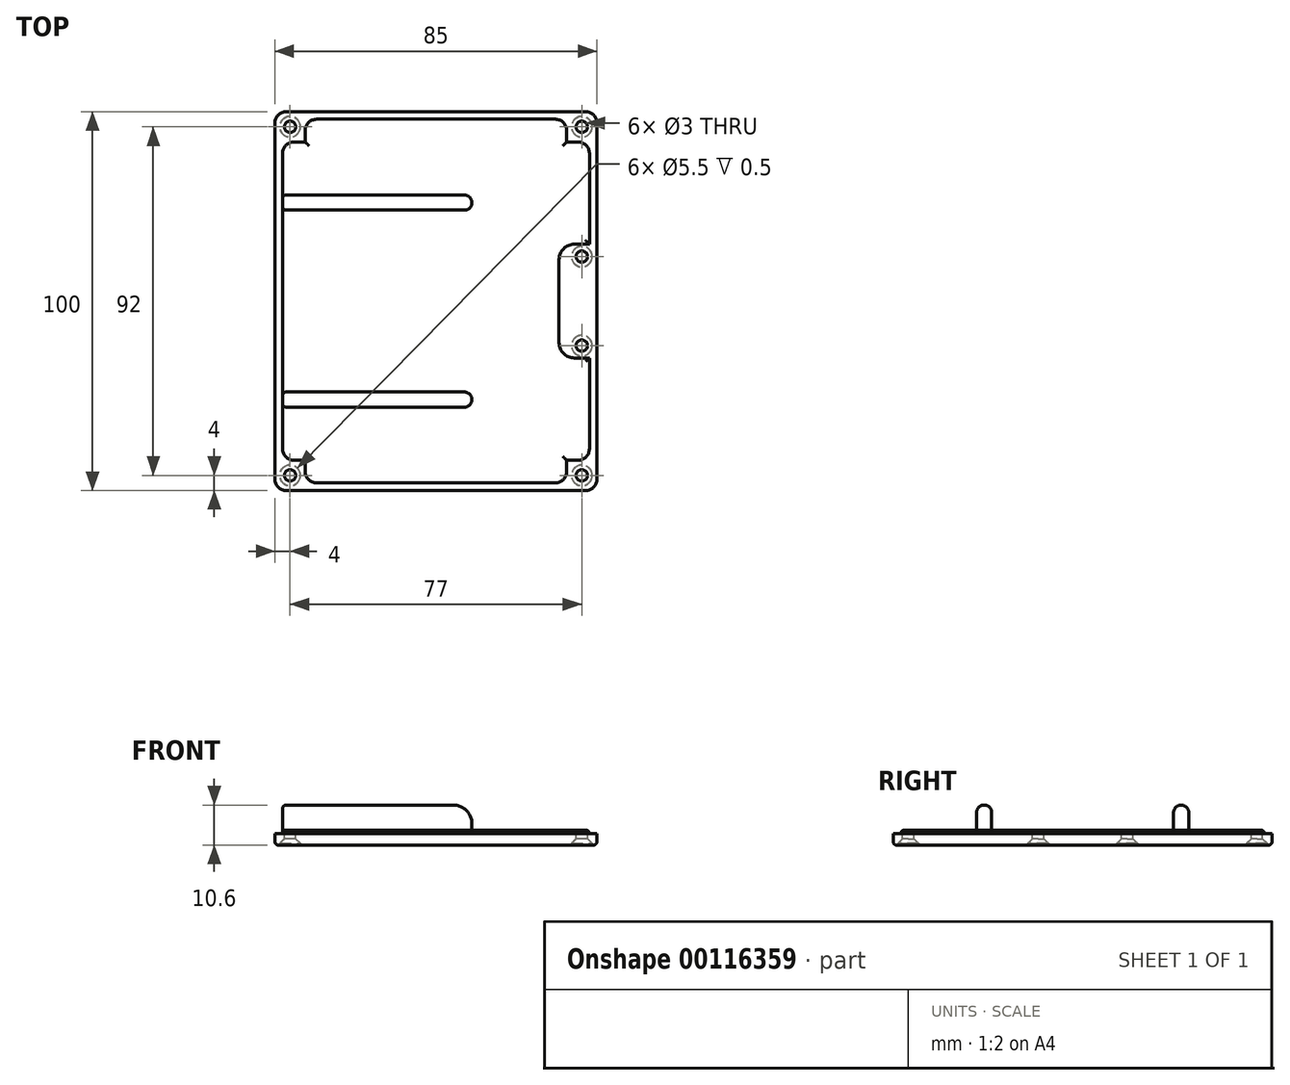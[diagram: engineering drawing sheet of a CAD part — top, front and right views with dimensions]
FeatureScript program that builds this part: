
annotation { "Feature Type Name" : "Feature", "Feature Type Description" : "" }
export const myFeature = defineFeature(function(context is Context, id is Id, definition is map)
    precondition{}
    {
        {
            var Q0;
            Q0=qCreatedBy(makeId("Top.planeOp"),FACE);
            var sketch = newSketch(context, id + "F0", { "sketchPlane" : qUnion([Q0])});
            skLineSegment(sketch, "E0.bottom", {"start": v(3, 0) * mm, "end": v(82, 0) * mm});
            skLineSegment(sketch, "E0.top", {"start": v(3, 100) * mm, "end": v(82, 100) * mm});
            skLineSegment(sketch, "E0.left", {"start": v(0, 3) * mm, "end": v(0, 97) * mm});
            skLineSegment(sketch, "E0.right", {"start": v(85, 3) * mm, "end": v(85, 97) * mm});
            skPoint(sketch, "E1.visualSharp", {"position": v(0, 100) * mm});
            skArc(sketch, "E1.filletArc", {"start": v(3, 100) * mm, "mid": v(0.88, 99.12) * mm, "end": v(0, 97) * mm});
            skPoint(sketch, "E2.visualSharp", {"position": v(85, 100) * mm});
            skArc(sketch, "E2.filletArc", {"start": v(85, 97) * mm, "mid": v(84.12, 99.12) * mm, "end": v(82, 100) * mm});
            skPoint(sketch, "E3.visualSharp", {"position": v(85, 0) * mm});
            skArc(sketch, "E3.filletArc", {"start": v(82, 0) * mm, "mid": v(84.12, 0.88) * mm, "end": v(85, 3) * mm});
            skPoint(sketch, "E4.visualSharp", {"position": v(0, 0) * mm});
            skArc(sketch, "E4.filletArc", {"start": v(0, 3) * mm, "mid": v(0.88, 0.88) * mm, "end": v(3, 0) * mm});
            skSolve(sketch);
        }
        {
            var Q0;
            Q0=makeQuery(id+"F0.imprint","IMPRINT",FACE,{"disambiguationData":[TD([[makeQuery(id+"F0.imprint","IMPRINT",EDGE,{"derivedFrom":sQuery(id+"F0.wireOp",EDGE,"E0.bottom")}),1.0]])]});
            extrude(context, id + "F1", {"entities" : qUnion([Q0]), "depth" : 3 * mm});
        }
        {
            var Q0;
            Q0=makeQuery(id+"F1.opExtrude","CAP_FACE",FACE,{"disambiguationData":[OSD([sQuery(id+"F0.wireOp",EDGE,"E0.bottom"),sQuery(id+"F0.wireOp",EDGE,"E0.top"),sQuery(id+"F0.wireOp",EDGE,"E0.left"),sQuery(id+"F0.wireOp",EDGE,"E0.right"),sQuery(id+"F0.wireOp",EDGE,"E1.filletArc"),sQuery(id+"F0.wireOp",EDGE,"E2.filletArc"),sQuery(id+"F0.wireOp",EDGE,"E3.filletArc"),sQuery(id+"F0.wireOp",EDGE,"E4.filletArc")])],"isStart":false});
            var sketch = newSketch(context, id + "F2", { "sketchPlane" : qUnion([Q0])});
            skCircle(sketch, "E5", {"center": v(4, 96) * mm, "radius": 1.5 * mm});
            skCircle(sketch, "E6", {"center": v(81, 96) * mm, "radius": 1.5 * mm});
            skCircle(sketch, "E7", {"center": v(81, 4) * mm, "radius": 1.5 * mm});
            skCircle(sketch, "E8", {"center": v(4, 4) * mm, "radius": 1.5 * mm});
            skCircle(sketch, "E9", {"center": v(81, 61.75) * mm, "radius": 1.5 * mm});
            skCircle(sketch, "E10", {"center": v(81, 38.25) * mm, "radius": 1.5 * mm});
            skSolve(sketch);
        }
        {
            var Q0;
            Q0=makeQuery(id+"F2.imprint","IMPRINT",FACE,{"disambiguationData":[TD([[makeQuery(id+"F2.imprint","IMPRINT",EDGE,{"derivedFrom":sQuery(id+"F2.wireOp",EDGE,"E5")}),1.0]])]});
            var Q1;
            Q1=makeQuery(id+"F2.imprint","IMPRINT",FACE,{"disambiguationData":[TD([[makeQuery(id+"F2.imprint","IMPRINT",EDGE,{"derivedFrom":sQuery(id+"F2.wireOp",EDGE,"E6")}),1.0]])]});
            var Q2;
            Q2=makeQuery(id+"F2.imprint","IMPRINT",FACE,{"disambiguationData":[TD([[makeQuery(id+"F2.imprint","IMPRINT",EDGE,{"derivedFrom":sQuery(id+"F2.wireOp",EDGE,"E8")}),1.0]])]});
            var Q3;
            Q3=makeQuery(id+"F2.imprint","IMPRINT",FACE,{"disambiguationData":[TD([[makeQuery(id+"F2.imprint","IMPRINT",EDGE,{"derivedFrom":sQuery(id+"F2.wireOp",EDGE,"E7")}),1.0]])]});
            var Q4;
            Q4=makeQuery(id+"F2.imprint","IMPRINT",FACE,{"disambiguationData":[TD([[makeQuery(id+"F2.imprint","IMPRINT",EDGE,{"derivedFrom":sQuery(id+"F2.wireOp",EDGE,"E9")}),1.0]])]});
            var Q5;
            Q5=makeQuery(id+"F2.imprint","IMPRINT",FACE,{"disambiguationData":[TD([[makeQuery(id+"F2.imprint","IMPRINT",EDGE,{"derivedFrom":sQuery(id+"F2.wireOp",EDGE,"E10")}),1.0]])]});
            extrude(context, id + "F3", {"entities" : qUnion([Q0, Q1, Q2, Q3, Q4, Q5]), "operationType" : NewBodyOperationType.REMOVE, "oppositeDirection" : true, "depth" : 5 * mm});
        }
        {
            var Q0;
            Q0=makeQuery(id+"F1.opExtrude","CAP_FACE",FACE,{"disambiguationData":[OSD([sQuery(id+"F0.wireOp",EDGE,"E0.bottom"),sQuery(id+"F0.wireOp",EDGE,"E0.top"),sQuery(id+"F0.wireOp",EDGE,"E0.left"),sQuery(id+"F0.wireOp",EDGE,"E0.right"),sQuery(id+"F0.wireOp",EDGE,"E1.filletArc"),sQuery(id+"F0.wireOp",EDGE,"E2.filletArc"),sQuery(id+"F0.wireOp",EDGE,"E3.filletArc"),sQuery(id+"F0.wireOp",EDGE,"E4.filletArc")])],"isStart":false});
            var sketch = newSketch(context, id + "F4", { "sketchPlane" : qUnion([Q0])});
            skLineSegment(sketch, "E11.1", {"start": v(11, 2) * mm, "end": v(74, 2) * mm});
            skLineSegment(sketch, "E11.2", {"start": v(2, 11) * mm, "end": v(2, 89) * mm});
            skLineSegment(sketch, "E11.5", {"start": v(11, 98) * mm, "end": v(74, 98) * mm});
            skLineSegment(sketch, "E11.7", {"start": v(83, 11) * mm, "end": v(83, 35) * mm});
            skLineSegment(sketch, "E12.top", {"start": v(5, 92) * mm, "end": v(8, 92) * mm});
            skLineSegment(sketch, "E12.right", {"start": v(8, 95) * mm, "end": v(8, 92) * mm});
            skLineSegment(sketch, "E13.top", {"start": v(80, 92) * mm, "end": v(77, 92) * mm});
            skLineSegment(sketch, "E13.right", {"start": v(77, 95) * mm, "end": v(77, 92) * mm});
            skLineSegment(sketch, "E14.top", {"start": v(80, 8) * mm, "end": v(77, 8) * mm});
            skLineSegment(sketch, "E14.right", {"start": v(77, 5) * mm, "end": v(77, 8) * mm});
            skLineSegment(sketch, "E15.top", {"start": v(5, 8) * mm, "end": v(8, 8) * mm});
            skLineSegment(sketch, "E15.right", {"start": v(8, 5) * mm, "end": v(8, 8) * mm});
            skPoint(sketch, "E16.visualSharp", {"position": v(2, 92) * mm});
            skArc(sketch, "E16.filletArc", {"start": v(5, 92) * mm, "mid": v(2.88, 91.12) * mm, "end": v(2, 89) * mm});
            skPoint(sketch, "E17.visualSharp", {"position": v(8, 98) * mm});
            skArc(sketch, "E17.filletArc", {"start": v(11, 98) * mm, "mid": v(8.88, 97.12) * mm, "end": v(8, 95) * mm});
            skPoint(sketch, "E18.visualSharp", {"position": v(77, 98) * mm});
            skArc(sketch, "E18.filletArc", {"start": v(77, 95) * mm, "mid": v(76.12, 97.12) * mm, "end": v(74, 98) * mm});
            skPoint(sketch, "E19.visualSharp", {"position": v(83, 92) * mm});
            skArc(sketch, "E19.filletArc", {"start": v(83, 89) * mm, "mid": v(82.12, 91.12) * mm, "end": v(80, 92) * mm});
            skPoint(sketch, "E20.visualSharp", {"position": v(83, 8) * mm});
            skArc(sketch, "E20.filletArc", {"start": v(80, 8) * mm, "mid": v(82.12, 8.88) * mm, "end": v(83, 11) * mm});
            skPoint(sketch, "E21.visualSharp", {"position": v(77, 2) * mm});
            skArc(sketch, "E21.filletArc", {"start": v(74, 2) * mm, "mid": v(76.12, 2.88) * mm, "end": v(77, 5) * mm});
            skPoint(sketch, "E22.visualSharp", {"position": v(8, 2) * mm});
            skArc(sketch, "E22.filletArc", {"start": v(8, 5) * mm, "mid": v(8.88, 2.88) * mm, "end": v(11, 2) * mm});
            skPoint(sketch, "E23.visualSharp", {"position": v(2, 8) * mm});
            skArc(sketch, "E23.filletArc", {"start": v(2, 11) * mm, "mid": v(2.88, 8.88) * mm, "end": v(5, 8) * mm});
            skLineSegment(sketch, "E24.bottom", {"start": v(83, 50) * mm, "end": v(75, 50) * mm, "construction": true});
            skLineSegment(sketch, "E24.top", {"start": v(83, 65) * mm, "end": v(75, 65) * mm, "construction": true});
            skLineSegment(sketch, "E24.right", {"start": v(75, 50) * mm, "end": v(75, 65) * mm, "construction": true});
            skLineSegment(sketch, "E25.top", {"start": v(83, 35) * mm, "end": v(75, 35) * mm, "construction": true});
            skLineSegment(sketch, "E25.right", {"start": v(75, 50) * mm, "end": v(75, 35) * mm, "construction": true});
            skLineSegment(sketch, "E26.bottom", {"start": v(83, 65) * mm, "end": v(79, 65) * mm});
            skLineSegment(sketch, "E26.top", {"start": v(83, 35) * mm, "end": v(79, 35) * mm});
            skLineSegment(sketch, "E26.right", {"start": v(75, 61) * mm, "end": v(75, 39) * mm});
            skLineSegment(sketch, "E27.trimOffspring", {"start": v(83, 65) * mm, "end": v(83, 89) * mm});
            skPoint(sketch, "E28.visualSharp", {"position": v(75, 65) * mm});
            skArc(sketch, "E28.filletArc", {"start": v(79, 65) * mm, "mid": v(76.17, 63.83) * mm, "end": v(75, 61) * mm});
            skPoint(sketch, "E29.visualSharp", {"position": v(75, 35) * mm});
            skArc(sketch, "E29.filletArc", {"start": v(75, 39) * mm, "mid": v(76.17, 36.17) * mm, "end": v(79, 35) * mm});
            skSolve(sketch);
        }
        {
            var Q0;
            Q0=makeQuery(id+"F4.imprint","IMPRINT",FACE,{"disambiguationData":[TD([[makeQuery(id+"F4.imprint","IMPRINT",EDGE,{"derivedFrom":sQuery(id+"F4.wireOp",EDGE,"E11.1")}),1.0]])]});
            extrude(context, id + "F5", {"entities" : qUnion([Q0]), "operationType" : NewBodyOperationType.ADD, "depth" : 1 * mm});
        }
        {
            var Q0;
            Q0=makeQuery(id+"F1.opExtrude","CAP_EDGE",EDGE,{"disambiguationData":[OSD([sQuery(id+"F0.wireOp",EDGE,"E0.left")])],"isStart":true});
            fillet(context, id + "F6", {"entities" : qUnion([Q0]), "radius" : 1 * mm, "tangentPropagation" : true, "allowEdgeOverflow" : false});
        }
        {
            var Q0;
            Q0=makeQuery(id+"F1.opExtrude","CAP_FACE",FACE,{"disambiguationData":[OSD([sQuery(id+"F0.wireOp",EDGE,"E0.bottom"),sQuery(id+"F0.wireOp",EDGE,"E0.top"),sQuery(id+"F0.wireOp",EDGE,"E0.left"),sQuery(id+"F0.wireOp",EDGE,"E0.right"),sQuery(id+"F0.wireOp",EDGE,"E1.filletArc"),sQuery(id+"F0.wireOp",EDGE,"E2.filletArc"),sQuery(id+"F0.wireOp",EDGE,"E3.filletArc"),sQuery(id+"F0.wireOp",EDGE,"E4.filletArc")])],"isStart":true});
            var sketch = newSketch(context, id + "F7", { "sketchPlane" : qUnion([Q0])});
            skCircle(sketch, "E30", {"center": v(4, -4) * mm, "radius": 2.75 * mm});
            skCircle(sketch, "E31", {"center": v(81, -4) * mm, "radius": 2.75 * mm});
            skCircle(sketch, "E32", {"center": v(81, -96) * mm, "radius": 2.75 * mm});
            skCircle(sketch, "E33", {"center": v(4, -96) * mm, "radius": 2.75 * mm});
            skCircle(sketch, "E34", {"center": v(81, -61.75) * mm, "radius": 2.75 * mm});
            skCircle(sketch, "E35", {"center": v(81, -38.25) * mm, "radius": 2.75 * mm});
            skSolve(sketch);
        }
        {
            var Q0;
            Q0=qSketchRegion(id+"F7",true);
            extrude(context, id + "F8", {"entities" : qUnion([Q0]), "operationType" : NewBodyOperationType.REMOVE, "oppositeDirection" : true, "depth" : .5 * mm});
        }
        {
            var Q0;
            Q0=makeQuery(id+"F8.boolean.opBoolean","INTERSECT",EDGE,{"derivedFrom":[makeQuery(id+"F3.boolean.opBoolean","COPY",FACE,{"derivedFrom":makeQuery(id+"F3.opExtrude","SWEPT_FACE",FACE,{"disambiguationData":[OSD([sQuery(id+"F2.wireOp",EDGE,"E8")])]})}),makeQuery(id+"F8.opExtrude","CAP_FACE",FACE,{"disambiguationData":[OSD([sQuery(id+"F7.wireOp",EDGE,"E30")])],"isStart":false})]});
            var Q1;
            Q1=makeQuery(id+"F8.boolean.opBoolean","INTERSECT",EDGE,{"derivedFrom":[makeQuery(id+"F3.boolean.opBoolean","COPY",FACE,{"derivedFrom":makeQuery(id+"F3.opExtrude","SWEPT_FACE",FACE,{"disambiguationData":[OSD([sQuery(id+"F2.wireOp",EDGE,"E7")])]})}),makeQuery(id+"F8.opExtrude","CAP_FACE",FACE,{"disambiguationData":[OSD([sQuery(id+"F7.wireOp",EDGE,"E31")])],"isStart":false})]});
            var Q2;
            Q2=makeQuery(id+"F8.boolean.opBoolean","INTERSECT",EDGE,{"derivedFrom":[makeQuery(id+"F3.boolean.opBoolean","COPY",FACE,{"derivedFrom":makeQuery(id+"F3.opExtrude","SWEPT_FACE",FACE,{"disambiguationData":[OSD([sQuery(id+"F2.wireOp",EDGE,"E5")])]})}),makeQuery(id+"F8.opExtrude","CAP_FACE",FACE,{"disambiguationData":[OSD([sQuery(id+"F7.wireOp",EDGE,"E33")])],"isStart":false})]});
            var Q3;
            Q3=makeQuery(id+"F8.boolean.opBoolean","INTERSECT",EDGE,{"derivedFrom":[makeQuery(id+"F3.boolean.opBoolean","COPY",FACE,{"derivedFrom":makeQuery(id+"F3.opExtrude","SWEPT_FACE",FACE,{"disambiguationData":[OSD([sQuery(id+"F2.wireOp",EDGE,"E6")])]})}),makeQuery(id+"F8.opExtrude","CAP_FACE",FACE,{"disambiguationData":[OSD([sQuery(id+"F7.wireOp",EDGE,"E32")])],"isStart":false})]});
            var Q4;
            Q4=makeQuery(id+"F8.boolean.opBoolean","INTERSECT",EDGE,{"derivedFrom":[makeQuery(id+"F3.boolean.opBoolean","COPY",FACE,{"derivedFrom":makeQuery(id+"F3.opExtrude","SWEPT_FACE",FACE,{"disambiguationData":[OSD([sQuery(id+"F2.wireOp",EDGE,"E9")])]})}),makeQuery(id+"F8.opExtrude","CAP_FACE",FACE,{"disambiguationData":[OSD([sQuery(id+"F7.wireOp",EDGE,"E34")])],"isStart":false})]});
            var Q5;
            Q5=makeQuery(id+"F8.boolean.opBoolean","INTERSECT",EDGE,{"derivedFrom":[makeQuery(id+"F3.boolean.opBoolean","COPY",FACE,{"derivedFrom":makeQuery(id+"F3.opExtrude","SWEPT_FACE",FACE,{"disambiguationData":[OSD([sQuery(id+"F2.wireOp",EDGE,"E10")])]})}),makeQuery(id+"F8.opExtrude","CAP_FACE",FACE,{"disambiguationData":[OSD([sQuery(id+"F7.wireOp",EDGE,"E35")])],"isStart":false})]});
            chamfer(context, id + "F9", {"entities" : qUnion([Q0, Q1, Q2, Q3, Q4, Q5]), "chamferType" : ChamferType.OFFSET_ANGLE, "width" : 1.2 * mm, "oppositeDirection" : false, "angle" : 45 * degree, "tangentPropagation" : true});
        }
        {
            var Q0;
            Q0=makeQuery(id+"F5.opExtrude","CAP_FACE",FACE,{"disambiguationData":[OSD([sQuery(id+"F4.wireOp",EDGE,"E11.1"),sQuery(id+"F4.wireOp",EDGE,"E11.2"),sQuery(id+"F4.wireOp",EDGE,"E11.5"),sQuery(id+"F4.wireOp",EDGE,"E11.7"),sQuery(id+"F4.wireOp",EDGE,"E12.top"),sQuery(id+"F4.wireOp",EDGE,"E12.right"),sQuery(id+"F4.wireOp",EDGE,"E13.top"),sQuery(id+"F4.wireOp",EDGE,"E13.right"),sQuery(id+"F4.wireOp",EDGE,"E14.top"),sQuery(id+"F4.wireOp",EDGE,"E14.right"),sQuery(id+"F4.wireOp",EDGE,"E15.top"),sQuery(id+"F4.wireOp",EDGE,"E15.right"),sQuery(id+"F4.wireOp",EDGE,"E16.filletArc"),sQuery(id+"F4.wireOp",EDGE,"E17.filletArc"),sQuery(id+"F4.wireOp",EDGE,"E18.filletArc"),sQuery(id+"F4.wireOp",EDGE,"E19.filletArc"),sQuery(id+"F4.wireOp",EDGE,"E20.filletArc"),sQuery(id+"F4.wireOp",EDGE,"E21.filletArc"),sQuery(id+"F4.wireOp",EDGE,"E22.filletArc"),sQuery(id+"F4.wireOp",EDGE,"E23.filletArc"),sQuery(id+"F4.wireOp",EDGE,"E26.bottom"),sQuery(id+"F4.wireOp",EDGE,"E26.top"),sQuery(id+"F4.wireOp",EDGE,"E26.right"),sQuery(id+"F4.wireOp",EDGE,"E27.trimOffspring"),sQuery(id+"F4.wireOp",EDGE,"E28.filletArc"),sQuery(id+"F4.wireOp",EDGE,"E29.filletArc")])],"isStart":false});
            var sketch = newSketch(context, id + "F10", { "sketchPlane" : qUnion([Q0])});
            skLineSegment(sketch, "E36.bottom", {"start": v(2, 78) * mm, "end": v(52, 78) * mm});
            skLineSegment(sketch, "E36.top", {"start": v(2, 74) * mm, "end": v(52, 74) * mm});
            skLineSegment(sketch, "E36.left", {"start": v(2, 78) * mm, "end": v(2, 74) * mm});
            skLineSegment(sketch, "E36.right", {"start": v(52, 78) * mm, "end": v(52, 74) * mm});
            skLineSegment(sketch, "E37.bottom", {"start": v(2, 26) * mm, "end": v(52, 26) * mm});
            skLineSegment(sketch, "E37.top", {"start": v(2, 22) * mm, "end": v(52, 22) * mm});
            skLineSegment(sketch, "E37.left", {"start": v(2, 26) * mm, "end": v(2, 22) * mm});
            skLineSegment(sketch, "E37.right", {"start": v(52, 26) * mm, "end": v(52, 22) * mm});
            skSolve(sketch);
        }
        {
            var Q0;
            Q0=makeQuery(id+"F10.imprint","IMPRINT",FACE,{"disambiguationData":[TD([[makeQuery(id+"F10.imprint","IMPRINT",EDGE,{"derivedFrom":sQuery(id+"F10.wireOp",EDGE,"E36.bottom")}),-1.0]])]});
            var Q1;
            Q1=makeQuery(id+"F10.imprint","IMPRINT",FACE,{"disambiguationData":[TD([[makeQuery(id+"F10.imprint","IMPRINT",EDGE,{"derivedFrom":sQuery(id+"F10.wireOp",EDGE,"E37.bottom")}),-1.0]])]});
            extrude(context, id + "F11", {"entities" : qUnion([Q0, Q1]), "operationType" : NewBodyOperationType.ADD, "depth" : 6.6 * mm});
        }
        {
            var Q0;
            Q0=makeQuery(id+"F11.opExtrude","CAP_EDGE",EDGE,{"disambiguationData":[OSD([sQuery(id+"F10.wireOp",EDGE,"E36.right")])],"isStart":false});
            var Q1;
            Q1=makeQuery(id+"F11.opExtrude","CAP_EDGE",EDGE,{"disambiguationData":[OSD([sQuery(id+"F10.wireOp",EDGE,"E37.right")])],"isStart":false});
            fillet(context, id + "F12", {"entities" : qUnion([Q0, Q1]), "radius" : 5 * mm, "tangentPropagation" : true, "allowEdgeOverflow" : false});
        }
        {
            var Q0;
            Q0=makeQuery(id+"F11.opExtrude","CAP_EDGE",EDGE,{"disambiguationData":[OSD([sQuery(id+"F10.wireOp",EDGE,"E36.bottom")])],"isStart":false});
            var Q1;
            Q1=makeQuery(id+"F11.opExtrude","CAP_EDGE",EDGE,{"disambiguationData":[OSD([sQuery(id+"F10.wireOp",EDGE,"E36.top")])],"isStart":false});
            var Q2;
            Q2=makeQuery(id+"F11.opExtrude","CAP_EDGE",EDGE,{"disambiguationData":[OSD([sQuery(id+"F10.wireOp",EDGE,"E37.bottom")])],"isStart":false});
            var Q3;
            Q3=makeQuery(id+"F11.opExtrude","CAP_EDGE",EDGE,{"disambiguationData":[OSD([sQuery(id+"F10.wireOp",EDGE,"E37.top")])],"isStart":false});
            fillet(context, id + "F13", {"entities" : qUnion([Q0, Q1, Q2, Q3]), "radius" : 2 * mm, "tangentPropagation" : true, "allowEdgeOverflow" : false});
        }
        {
            var Q0;
            {var subQ0=sQuery(id+"F4.wireOp",EDGE,"E11.2");Q0=makeQuery(id+"F11.boolean.opBoolean","SPLIT",EDGE,{"disambiguationData":[TD([makeQuery(id+"F11.opExtrude","SWEPT_FACE",FACE,{"disambiguationData":[OSD([sQuery(id+"F10.wireOp",EDGE,"E36.top")])]})])],"derivedFrom":makeQuery(id+"F5.opExtrude","CAP_EDGE",EDGE,{"disambiguationData":[OSD([subQ0])],"isStart":false})});}
            var Q1;
            Q1=makeQuery(id+"F5.opExtrude","CAP_EDGE",EDGE,{"disambiguationData":[OSD([sQuery(id+"F4.wireOp",EDGE,"E11.1")])],"isStart":false});
            var Q2;
            Q2=makeQuery(id+"F5.opExtrude","CAP_EDGE",EDGE,{"disambiguationData":[OSD([sQuery(id+"F4.wireOp",EDGE,"E11.7")])],"isStart":false});
            var Q3;
            Q3=makeQuery(id+"F5.opExtrude","CAP_EDGE",EDGE,{"disambiguationData":[OSD([sQuery(id+"F4.wireOp",EDGE,"E27.trimOffspring")])],"isStart":false});
            var Q4;
            Q4=makeQuery(id+"F5.opExtrude","CAP_EDGE",EDGE,{"disambiguationData":[OSD([sQuery(id+"F4.wireOp",EDGE,"E11.5")])],"isStart":false});
            var Q5;
            Q5=makeQuery(id+"F5.opExtrude","CAP_EDGE",EDGE,{"disambiguationData":[OSD([sQuery(id+"F4.wireOp",EDGE,"E26.right")])],"isStart":false});
            var Q6;
            {var subQ0=sQuery(id+"F4.wireOp",EDGE,"E23.filletArc");var subQ1=sQuery(id+"F4.wireOp",EDGE,"E11.2");Q6=makeQuery(id+"F11.boolean.opBoolean","SPLIT",EDGE,{"disambiguationData":[TD([makeQuery(id+"F5.opExtrude","SWEPT_FACE",FACE,{"disambiguationData":[OSD([subQ0])]})])],"derivedFrom":makeQuery(id+"F5.opExtrude","CAP_EDGE",EDGE,{"disambiguationData":[OSD([subQ1])],"isStart":false})});}
            var Q7;
            {var subQ0=sQuery(id+"F4.wireOp",EDGE,"E11.2");var subQ1=sQuery(id+"F4.wireOp",EDGE,"E16.filletArc");Q7=makeQuery(id+"F11.boolean.opBoolean","SPLIT",EDGE,{"disambiguationData":[TD([makeQuery(id+"F5.opExtrude","SWEPT_FACE",FACE,{"disambiguationData":[OSD([subQ1])]})])],"derivedFrom":makeQuery(id+"F5.opExtrude","CAP_EDGE",EDGE,{"disambiguationData":[OSD([subQ0])],"isStart":false})});}
            var Q8;
            Q8=makeQuery(id+"F11.opExtrude","SWEPT_EDGE",EDGE,{"disambiguationData":[OSD([sQuery(id+"F4.wireOp",EDGE,"E11.2"),sQuery(id+"F10.wireOp",EDGE,"E37.bottom"),sQuery(id+"F10.wireOp",EDGE,"E37.left")])]});
            var Q9;
            Q9=makeQuery(id+"F11.opExtrude","SWEPT_EDGE",EDGE,{"disambiguationData":[OSD([sQuery(id+"F4.wireOp",EDGE,"E11.2"),sQuery(id+"F10.wireOp",EDGE,"E36.bottom"),sQuery(id+"F10.wireOp",EDGE,"E36.left")])]});
            fillet(context, id + "F14", {"entities" : qUnion([Q0, Q1, Q2, Q3, Q4, Q5, Q6, Q7, Q8, Q9]), "radius" : 1 * mm, "tangentPropagation" : true, "allowEdgeOverflow" : false});
        }
    });
